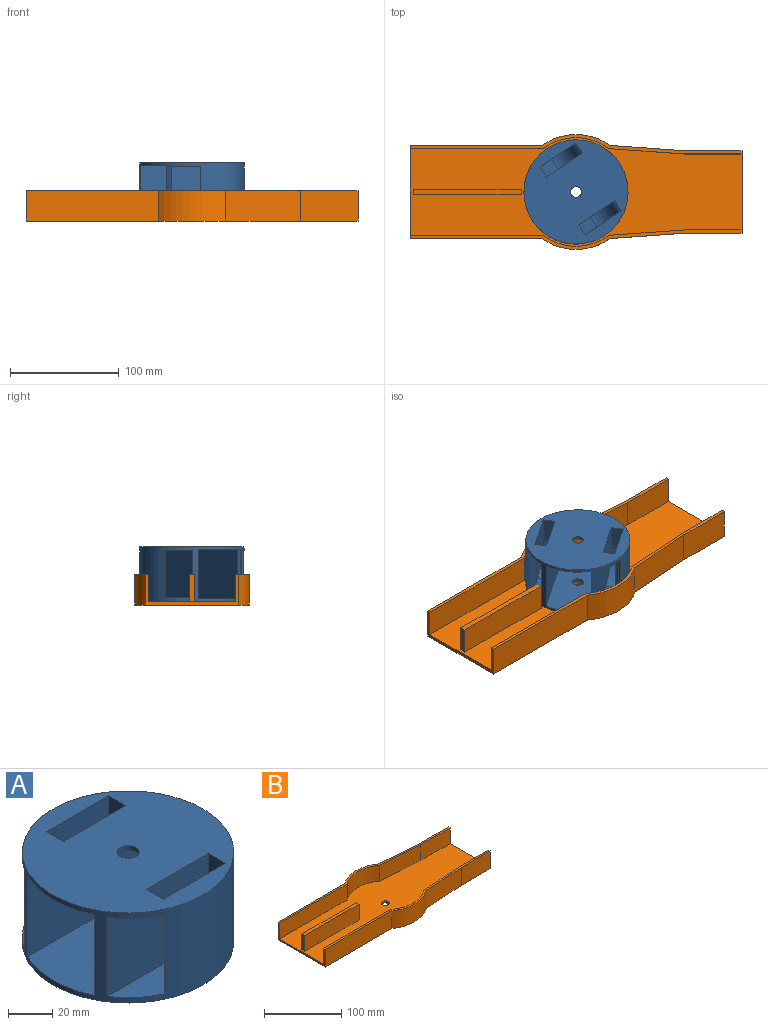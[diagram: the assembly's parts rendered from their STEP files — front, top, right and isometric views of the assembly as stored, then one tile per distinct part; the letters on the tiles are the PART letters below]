
ASSEMBLY  parts=2 mates=1
PART A: 27 faces, bbox 96x96x50 mm
  f0: cylinder r=48mm len=96mm, axis (0,0,1), area 8726.5mm2, adj f2,f4,f8,f9,f10,f11,f12,f14
  f1: cylinder r=5mm len=10mm, axis (0,0,1), area 78.5mm2, adj f4,f22
  f2: plane 96x96mm, normal (0,0,1), area 6279.7mm2, adj f0,f3,f5,f6,f7,f8,f13,f15
  f3: cylinder r=5mm len=10mm, axis (0,0,1), area 78.5mm2, adj f2,f21
  f4: plane 96x96mm, normal (0,0,-1), area 7159.7mm2, adj f0,f1
  f5: plane 11x3mm, normal (1,0,0), area 33mm2, adj f2,f6,f8,f10
  f6: plane 47x40mm, normal (0,1,0), area 1456.8mm2, adj f2,f5,f7,f10,f11,f23,f25
  f7: plane 20x11mm, normal (-1,0,0), area 220mm2, adj f2,f6,f8,f25
  f8: plane 65.04x47mm, normal (0,-1,0), area 2825.5mm2, adj f0,f2,f5,f7,f10,f11,f25
  f9: plane 44x1.45mm, normal (-0.77,0.64,0), area 83.2mm2, adj f0,f10,f11,f23
  f10: plane 31.11x17.09mm, normal (0,0,-1), area 279.4mm2, adj f0,f5,f6,f8,f9,f23
  f11: plane 38.04x17.09mm, normal (0,0,1), area 422.4mm2, adj f0,f6,f8,f9,f23,f25
  f12: plane 31.11x17.09mm, normal (0,0,-1), area 279.4mm2, adj f0,f13,f14,f15,f18,f24
  f13: plane 47x40mm, normal (0,-1,0), area 1456.8mm2, adj f2,f12,f16,f17,f18,f24,f26
  f14: plane 44x1.45mm, normal (-0.77,-0.64,0), area 83.2mm2, adj f0,f12,f17,f24
  f15: plane 65.04x47mm, normal (0,1,0), area 2825.5mm2, adj f0,f2,f12,f16,f17,f18,f26
  f16: plane 20x11mm, normal (-1,0,0), area 220mm2, adj f2,f13,f15,f26
  f17: plane 38.04x17.09mm, normal (0,0,1), area 422.4mm2, adj f0,f13,f14,f15,f24,f26
  f18: plane 11x3mm, normal (1,0,0), area 33mm2, adj f2,f12,f13,f15
  f19: plane 85.83x45mm, normal (0,-1,0), area 3862.4mm2, adj f0,f21,f22
  f20: plane 85.83x45mm, normal (0,1,0), area 3862.4mm2, adj f0,f21,f22
  f21: plane 96x43mm, normal (0,0,-1), area 3906.9mm2, adj f0,f3,f19,f20
  f22: plane 96x43mm, normal (0,0,1), area 3906.9mm2, adj f0,f1,f19,f20
  f23: cylinder r=13mm len=44mm, axis (0,0,1), area 499.2mm2, adj f6,f9,f10,f11
  f24: cylinder r=13mm len=44mm, axis (0,0,1), area 499.2mm2, adj f12,f13,f14,f17
  f25: cylinder r=27mm len=27mm, axis (0,-1,0), area 466.5mm2, adj f6,f7,f8,f11
  f26: cylinder r=27mm len=27mm, axis (0,-1,0), area 466.5mm2, adj f13,f15,f16,f17
PART B: 28 faces, bbox 306x106x28 mm
  f0: plane 306x100mm, normal (0,0,1), area 23841.5mm2, adj f1,f6,f11,f13,f14,f15,f16,f18
  f1: plane 76x28mm, normal (1,0,0), area 378mm2, adj f0,f2,f10,f12,f18,f22,f23,f27
  f2: plane 52.89x28mm, normal (0,1,0), area 1481mm2, adj f1,f3,f12,f22
  f3: plane 69.03x28mm, normal (0.07,1,0), area 1937.7mm2, adj f2,f4,f12,f22
  f4: cylinder r=53mm len=62.06mm, axis (0,0,1), area 1856.5mm2, adj f3,f5,f12,f22
  f5: plane 122.02x28mm, normal (0,1,0), area 3416.5mm2, adj f4,f6,f12,f22
  f6: plane 86x28mm, normal (-1,0,0), area 408mm2, adj f0,f5,f7,f12,f19,f22,f26,f27
  f7: plane 122.02x28mm, normal (0,-1,0), area 3416.5mm2, adj f6,f8,f12,f27
  f8: cylinder r=53mm len=62.06mm, axis (0,0,1), area 1856.5mm2, adj f7,f9,f12,f27
  f9: plane 69.03x28mm, normal (0.07,-1,0), area 1937.7mm2, adj f8,f10,f12,f27
  f10: plane 52.89x28mm, normal (0,-1,0), area 1481mm2, adj f1,f9,f12,f27
  f11: cylinder r=5mm len=10mm, axis (0,0,1), area 94.2mm2, adj f0,f12
  f12: plane 306x106mm, normal (0,0,-1), area 26201.8mm2, adj f1,f2,f3,f4,f5,f6,f7,f8
  f13: plane 99.5x25mm, normal (0,1,0), area 2487.5mm2, adj f0,f14,f16,f17
  f14: plane 25x5mm, normal (-1,0,0), area 125mm2, adj f0,f13,f15,f17
  f15: plane 99.5x25mm, normal (0,-1,0), area 2487.5mm2, adj f0,f14,f16,f17
  f16: plane 25x5mm, normal (1,0,0), area 125mm2, adj f0,f13,f15,f17
  f17: plane 99.5x5mm, normal (0,0,1), area 497.5mm2, adj f13,f14,f15,f16
  f18: plane 53x25mm, normal (0,-1,0), area 1325mm2, adj f0,f1,f21,f22
  f19: plane 123x25mm, normal (0,-1,0), area 3075mm2, adj f0,f6,f20,f22
  f20: cylinder r=50mm len=60mm, axis (0,0,-1), area 1608.8mm2, adj f0,f19,f21,f22
  f21: plane 70x25mm, normal (-0.07,-1,0), area 1754.5mm2, adj f0,f18,f20,f22
  f22: plane 306x18mm, normal (0,0,1), area 931.4mm2, adj f1,f2,f3,f4,f5,f6,f18,f19
  f23: plane 53x25mm, normal (0,1,0), area 1325mm2, adj f0,f1,f24,f27
  f24: plane 70x25mm, normal (-0.07,1,0), area 1754.5mm2, adj f0,f23,f25,f27
  f25: cylinder r=50mm len=60mm, axis (0,0,-1), area 1608.8mm2, adj f0,f24,f26,f27
  f26: plane 123x25mm, normal (0,1,0), area 3075mm2, adj f0,f6,f25,f27
  f27: plane 306x18mm, normal (0,0,1), area 931.4mm2, adj f1,f6,f7,f8,f9,f10,f23,f24
PLACE A rot(axis=(0,0,1),33.9deg) t=(-152.69,38.33,28.71)mm
PLACE B t=(-152.69,38.33,31.21)mm fixed
MATE revolute A.f0 <-> B.f11  axis (0,0,1) through (-152.69,38.33,28.71)mm
